# Revit family: Hager-SM_Design_10-Switch_Disc.Incomer-NoHosted-UK-en
name_source: partatom
category: Electrical Equipment
units: mm (PartAtom-declared; Revit-internal decimal feet)

## family parameters
Always vertical = Yes
Cut with Voids When Loaded = No
Panel Configuration = Two Columns, Circuits Across
Part Type = Panelboard
Room Calculation Point = No
Round Connector Dimension = Use Diameter
Shared = No
Work Plane-Based = Yes

## types (7) — shared parameters
Classification.Uniclass.Pr.Description = Control circuit device enclosures
Classification.Uniclass.Pr.Number = Pr_80_77_28_16
Default Elevation = 1219 mm
EF000003 - Mounting method = EV000384 - Surface mounted (plaster)
EF000007 - Colour = EV000202 - White
EF000116 - RAL-number = 9010
EF000118 - With mounting plate = No
EF000266 - Number of rows = 1
EF000339 - Type of cover = EV004216 - Door
EF001062 - EMC-version = No
EF001134 - DIN-rail = No
EF001596 - Material housing = EV000179 - Steel
EF004462 - Type of closure = EV000154 - Other
EF005474 - Degree of protection (IP) = EV009848 - IP2XC
EF006244 - Transparent cover/door = No
EF006306 - With lock = No
EF015776 - Earthing terminal block = Yes
EF015777 - Neutral terminal block = Yes
EF015941 - Signal passing door = No
HG000002 - With door or cover = Yes
HG000003 - Range = Surface Mounting Consumer Units
HG000005 - Thickness = 3 mm  [stored 0.00984252 ft]
HG000006 - Flush mounted = No
HG000017 - Distance between poles = 18 mm  [stored 0.0590551 ft]
Manufacturer = Hager
Type Comments = Surface Mounting Consumer Units
zero-valued in all types: Cost, EF000218 - Built-in depth, EF000332 - Built-in height, EF000846 - Built-in width, EF001131 - Internal depth

## per-type parameters (varying)
| type | EF000008 - Width | EF000040 - Height | EF000049 - Depth | EF001088 - Extension possible | EF002950 - Width in number of modular spacings | EF009212 - Cover model | HG000004 - Manufacturer reference | Model |
| Surface mounted P2XC W154 H245 D98.2 4 Modular spacings - VML004 | 154 mm  [stored 0.505249 ft] | 245 mm  [stored 0.803806 ft] | 98 mm  [stored 0.321522 ft] | No | 4 |  | VML004 | VML004 |
| Surface mounted P2XC W225 H245 D98.2 8 Modular spacings - VML008 | 225 mm  [stored 0.738189 ft] | 245 mm  [stored 0.803806 ft] | 98 mm  [stored 0.321522 ft] | No | 8 |  | VML008 | VML008 |
| Surface mounted P2XC W297 H245 D98.2 12 Modular spacings - VML012 | 297 mm  [stored 0.974409 ft] | 245 mm  [stored 0.803806 ft] | 98 mm  [stored 0.321522 ft] | No | 12 |  | VML012 | VML012 |
| Surface mounted P2XC W368.4 H245 D98.2 16 Modular spacings - VML016 | 368 mm  [stored 1.20735 ft] | 245 mm  [stored 0.803806 ft] | 98 mm  [stored 0.321522 ft] | No | 16 |  | VML016 | VML016 |
| Surface mounted P2XC W370 H246 D100 12 Modular spacings - VML112SPD | 370 mm  [stored 1.21391 ft] | 246 mm  [stored 0.807087 ft] | 100 mm  [stored 0.328084 ft] | Yes | 12 | EV000116 - Closed | VML112SPD | VML112SPD |
| Surface mounted P2XC W478 H245 D98.2 18 Modular spacings - VML018 | 478 mm  [stored 1.56824 ft] | 245 mm  [stored 0.803806 ft] | 98 mm  [stored 0.321522 ft] | No | 18 |  | VML018 | VML018 |
| Surface mounted P2XC W478 H245 D98.2 22 Modular spacings - VML022 | 478 mm  [stored 1.56824 ft] | 245 mm  [stored 0.803806 ft] | 98 mm  [stored 0.321522 ft] | No | 22 |  | VML022 | VML022 |

note: [stored X ft] marks values corroborated as IEEE doubles in the binary element streams (Revit-internal decimal feet)

## geometry (parser evidence)
native form markers: Blend x4, Sweep x15
no freeform markers — native parametric forms only
